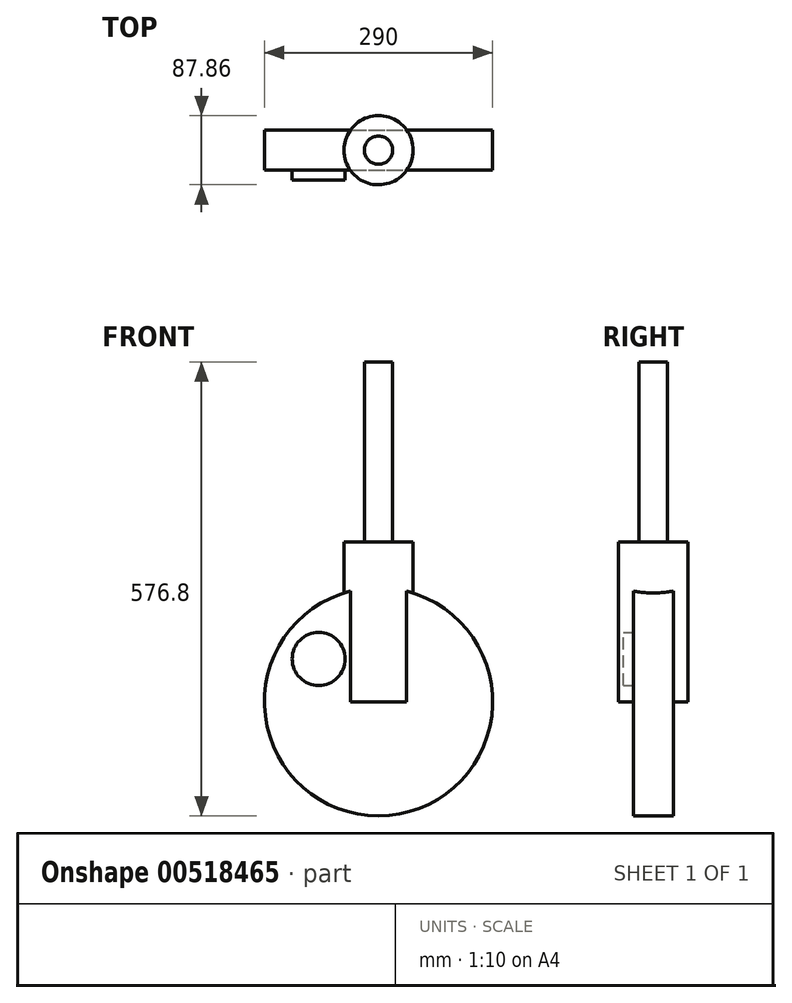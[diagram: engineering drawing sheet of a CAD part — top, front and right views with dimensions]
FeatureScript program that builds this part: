
annotation { "Feature Type Name" : "Feature", "Feature Type Description" : "" }
export const myFeature = defineFeature(function(context is Context, id is Id, definition is map)
    precondition{}
    {
        {
            var Q0;
            Q0=qCreatedBy(makeId("Top.planeOp"),FACE);
            var sketch = newSketch(context, id + "F0", { "sketchPlane" : qUnion([Q0])});
            skCircle(sketch, "E0", {"center": v(0, 0) * mm, "radius": 43.93 * mm});
            skSolve(sketch);
        }
        {
            var Q0;
            Q0=makeQuery(id+"F0.imprint","IMPRINT",FACE,{"disambiguationData":[TD([[makeQuery(id+"F0.imprint","IMPRINT",EDGE,{"derivedFrom":sQuery(id+"F0.wireOp",EDGE,"E0")}),1.0]])]});
            extrude(context, id + "F1", {"entities" : qUnion([Q0]), "depth" : 203.2 * mm, "offsetDistance" : 25.4 * mm});
        }
        {
            var Q0;
            Q0=makeQuery(id+"F1.opExtrude","CAP_FACE",FACE,{"disambiguationData":[OSD([sQuery(id+"F0.wireOp",EDGE,"E0")])],"isStart":false});
            var sketch = newSketch(context, id + "F2", { "sketchPlane" : qUnion([Q0])});
            skCircle(sketch, "E1", {"center": v(0, 0) * mm, "radius": 17.93 * mm});
            skSolve(sketch);
        }
        {
            var Q0;
            Q0=makeQuery(id+"F2.imprint","IMPRINT",FACE,{"disambiguationData":[TD([[makeQuery(id+"F2.imprint","IMPRINT",EDGE,{"derivedFrom":sQuery(id+"F2.wireOp",EDGE,"E1")}),1.0]])]});
            extrude(context, id + "F3", {"entities" : qUnion([Q0]), "operationType" : NewBodyOperationType.ADD, "depth" : 228.6 * mm, "offsetDistance" : 25.4 * mm});
        }
        {
            var Q0;
            Q0=qCreatedBy(makeId("Front.planeOp"),FACE);
            var sketch = newSketch(context, id + "F4", { "sketchPlane" : qUnion([Q0])});
            skCircle(sketch, "E2", {"center": v(0, 0) * mm, "radius": 145 * mm});
            skSolve(sketch);
        }
        {
            var Q0;
            Q0=makeQuery(id+"F4.imprint","IMPRINT",FACE,{"disambiguationData":[TD([[makeQuery(id+"F4.imprint","IMPRINT",EDGE,{"derivedFrom":sQuery(id+"F4.wireOp",EDGE,"E2")}),1.0]])]});
            extrude(context, id + "F5", {"entities" : qUnion([Q0]), "operationType" : NewBodyOperationType.ADD, "endBound" : BoundingType.SYMMETRIC, "oppositeDirection" : true, "depth" : 50.8 * mm, "offsetDistance" : 25.4 * mm});
        }
        {
            var Q0;
            Q0=makeQuery(id+"F5.opExtrude","CAP_FACE",FACE,{"disambiguationData":[OSD([sQuery(id+"F4.wireOp",EDGE,"E2")])],"isStart":true});
            var sketch = newSketch(context, id + "F6", { "sketchPlane" : qUnion([Q0])});
            skCircle(sketch, "E3", {"center": v(-76.07, 54.4) * mm, "radius": 33.66 * mm});
            skSolve(sketch);
        }
        {
            var Q0;
            Q0=makeQuery(id+"F6.imprint","IMPRINT",FACE,{"disambiguationData":[TD([[makeQuery(id+"F6.imprint","IMPRINT",EDGE,{"derivedFrom":sQuery(id+"F6.wireOp",EDGE,"E3")}),1.0]])]});
            extrude(context, id + "F7", {"entities" : qUnion([Q0]), "operationType" : NewBodyOperationType.ADD, "endBound" : BoundingType.SYMMETRIC, "depth" : 25.4 * mm, "offsetDistance" : 25.4 * mm});
        }
    });
